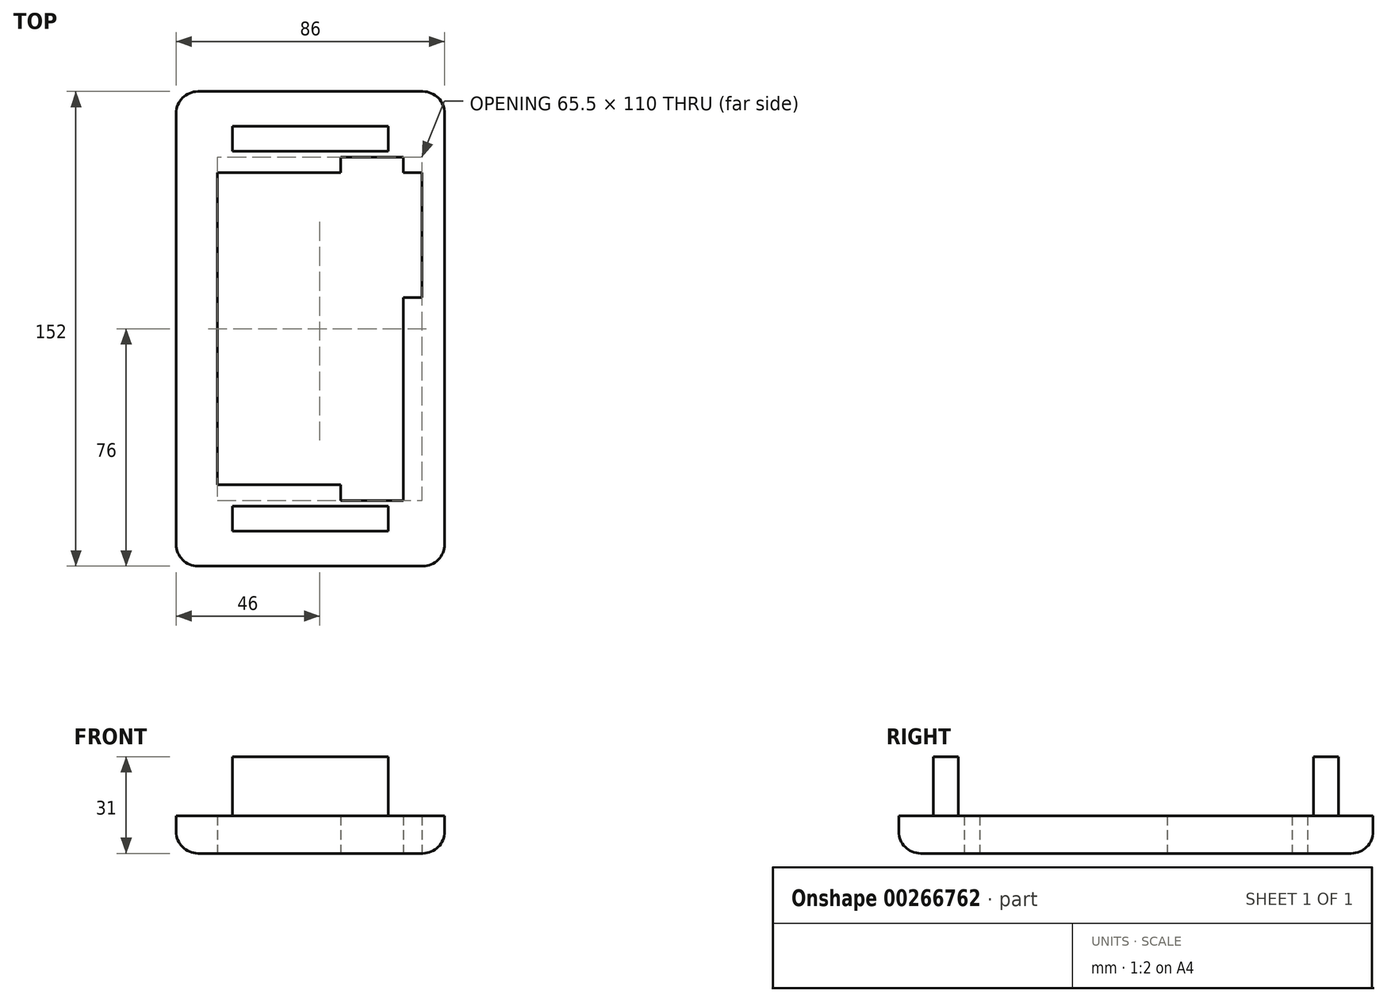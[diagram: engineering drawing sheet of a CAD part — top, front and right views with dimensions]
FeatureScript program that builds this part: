
annotation { "Feature Type Name" : "Feature", "Feature Type Description" : "" }
export const myFeature = defineFeature(function(context is Context, id is Id, definition is map)
    precondition{}
    {
        {
            var Q0;
            Q0=qCreatedBy(makeId("Top.planeOp"),FACE);
            var sketch = newSketch(context, id + "F0", { "sketchPlane" : qUnion([Q0])});
            skLineSegment(sketch, "E0.bottom", {"start": v(-43, 76) * mm, "end": v(43, 76) * mm});
            skLineSegment(sketch, "E0.top", {"start": v(-43, -76) * mm, "end": v(43, -76) * mm});
            skLineSegment(sketch, "E0.left", {"start": v(-43, 76) * mm, "end": v(-43, -76) * mm});
            skLineSegment(sketch, "E0.right", {"start": v(43, 76) * mm, "end": v(43, -76) * mm});
            skPoint(sketch, "E0.middle", {"position": v(0, 0) * mm});
            skLineSegment(sketch, "E1.bottom", {"start": v(-29.75, 50) * mm, "end": v(29.75, 50) * mm});
            skLineSegment(sketch, "E1.top", {"start": v(-29.75, -50) * mm, "end": v(29.75, -50) * mm});
            skLineSegment(sketch, "E1.left", {"start": v(-29.75, 50) * mm, "end": v(-29.75, -50) * mm});
            skLineSegment(sketch, "E1.right", {"start": v(29.75, 50) * mm, "end": v(29.75, -50) * mm});
            skLineSegment(sketch, "E2.bottom", {"start": v(29.75, 50) * mm, "end": v(35.75, 50) * mm});
            skLineSegment(sketch, "E2.top", {"start": v(29.75, 10) * mm, "end": v(35.75, 10) * mm});
            skLineSegment(sketch, "E2.left", {"start": v(29.75, 50) * mm, "end": v(29.75, 10) * mm});
            skLineSegment(sketch, "E2.right", {"start": v(35.75, 50) * mm, "end": v(35.75, 10) * mm});
            skLineSegment(sketch, "E3.bottom", {"start": v(-25, -64.85) * mm, "end": v(25, -64.85) * mm});
            skLineSegment(sketch, "E3.top", {"start": v(-25, -56.85) * mm, "end": v(25, -56.85) * mm});
            skLineSegment(sketch, "E3.left", {"start": v(-25, -64.85) * mm, "end": v(-25, -56.85) * mm});
            skLineSegment(sketch, "E3.right", {"start": v(25, -64.85) * mm, "end": v(25, -56.85) * mm});
            skPoint(sketch, "E3.middle", {"position": v(0, -60.85) * mm});
            skLineSegment(sketch, "E4.MirrorCS", {"start": v(-25, 56.85) * mm, "end": v(25, 56.85) * mm});
            skLineSegment(sketch, "E5.MirrorCS", {"start": v(-25, 64.85) * mm, "end": v(-25, 56.85) * mm});
            skLineSegment(sketch, "E6.MirrorCS", {"start": v(25, 64.85) * mm, "end": v(25, 56.85) * mm});
            skPoint(sketch, "E7.MirrorP", {"position": v(0, 60.85) * mm});
            skLineSegment(sketch, "E8.MirrorCS", {"start": v(-25, 64.85) * mm, "end": v(25, 64.85) * mm});
            skLineSegment(sketch, "E9.bottom", {"start": v(29.75, 50) * mm, "end": v(9.75, 50) * mm});
            skLineSegment(sketch, "E9.top", {"start": v(29.75, 55) * mm, "end": v(9.75, 55) * mm});
            skLineSegment(sketch, "E9.left", {"start": v(29.75, 50) * mm, "end": v(29.75, 55) * mm});
            skLineSegment(sketch, "E9.right", {"start": v(9.75, 50) * mm, "end": v(9.75, 55) * mm});
            skLineSegment(sketch, "E10.MirrorCS", {"start": v(9.75, -50) * mm, "end": v(9.75, -55) * mm});
            skLineSegment(sketch, "E11.MirrorCS", {"start": v(29.75, -55) * mm, "end": v(9.75, -55) * mm});
            skLineSegment(sketch, "E12.MirrorCS", {"start": v(29.75, -50) * mm, "end": v(29.75, -55) * mm});
            skSolve(sketch);
        }
        {
            var Q0;
            Q0=makeQuery(id+"F0.imprint","IMPRINT",FACE,{"disambiguationData":[TD([[makeQuery(id+"F0.imprint","IMPRINT",EDGE,{"derivedFrom":sQuery(id+"F0.wireOp",EDGE,"E0.bottom")}),-1.0]])]});
            extrude(context, id + "F1", {"entities" : qUnion([Q0]), "depth" : 12 * mm});
        }
        {
            var Q0;
            Q0=makeQuery(id+"F0.imprint","IMPRINT",FACE,{"disambiguationData":[TD([[makeQuery(id+"F0.imprint","IMPRINT",EDGE,{"derivedFrom":sQuery(id+"F0.wireOp",EDGE,"E4.MirrorCS")}),1.0]])]});
            var Q1;
            Q1=makeQuery(id+"F0.imprint","IMPRINT",FACE,{"disambiguationData":[TD([[makeQuery(id+"F0.imprint","IMPRINT",EDGE,{"derivedFrom":sQuery(id+"F0.wireOp",EDGE,"E3.bottom")}),1.0]])]});
            extrude(context, id + "F2", {"entities" : qUnion([Q0, Q1]), "operationType" : NewBodyOperationType.ADD, "depth" : 31 * mm});
        }
        {
            var Q0;
            Q0=makeQuery(id+"F1.opExtrude","SWEPT_EDGE",EDGE,{"disambiguationData":[OSD([sQuery(id+"F0.wireOp",EDGE,"E0.top"),sQuery(id+"F0.wireOp",EDGE,"E0.left")])]});
            var Q1;
            Q1=makeQuery(id+"F1.opExtrude","SWEPT_EDGE",EDGE,{"disambiguationData":[OSD([sQuery(id+"F0.wireOp",EDGE,"E0.top"),sQuery(id+"F0.wireOp",EDGE,"E0.right")])]});
            var Q2;
            Q2=makeQuery(id+"F1.opExtrude","SWEPT_EDGE",EDGE,{"disambiguationData":[OSD([sQuery(id+"F0.wireOp",EDGE,"E0.bottom"),sQuery(id+"F0.wireOp",EDGE,"E0.right")])]});
            var Q3;
            Q3=makeQuery(id+"F1.opExtrude","SWEPT_EDGE",EDGE,{"disambiguationData":[OSD([sQuery(id+"F0.wireOp",EDGE,"E0.bottom"),sQuery(id+"F0.wireOp",EDGE,"E0.left")])]});
            var Q4;
            Q4=makeQuery(id+"F1.opExtrude","CAP_EDGE",EDGE,{"disambiguationData":[OSD([sQuery(id+"F0.wireOp",EDGE,"E0.right")])],"isStart":true});
            var Q5;
            Q5=makeQuery(id+"F1.opExtrude","CAP_EDGE",EDGE,{"disambiguationData":[OSD([sQuery(id+"F0.wireOp",EDGE,"E0.top")])],"isStart":true});
            var Q6;
            Q6=makeQuery(id+"F1.opExtrude","CAP_EDGE",EDGE,{"disambiguationData":[OSD([sQuery(id+"F0.wireOp",EDGE,"E0.left")])],"isStart":true});
            var Q7;
            Q7=makeQuery(id+"F1.opExtrude","CAP_EDGE",EDGE,{"disambiguationData":[OSD([sQuery(id+"F0.wireOp",EDGE,"E0.bottom")])],"isStart":true});
            fillet(context, id + "F3", {"entities" : qUnion([Q0, Q1, Q2, Q3, Q4, Q5, Q6, Q7]), "radius" : 7 * mm, "tangentPropagation" : true, "allowEdgeOverflow" : false});
        }
    });
